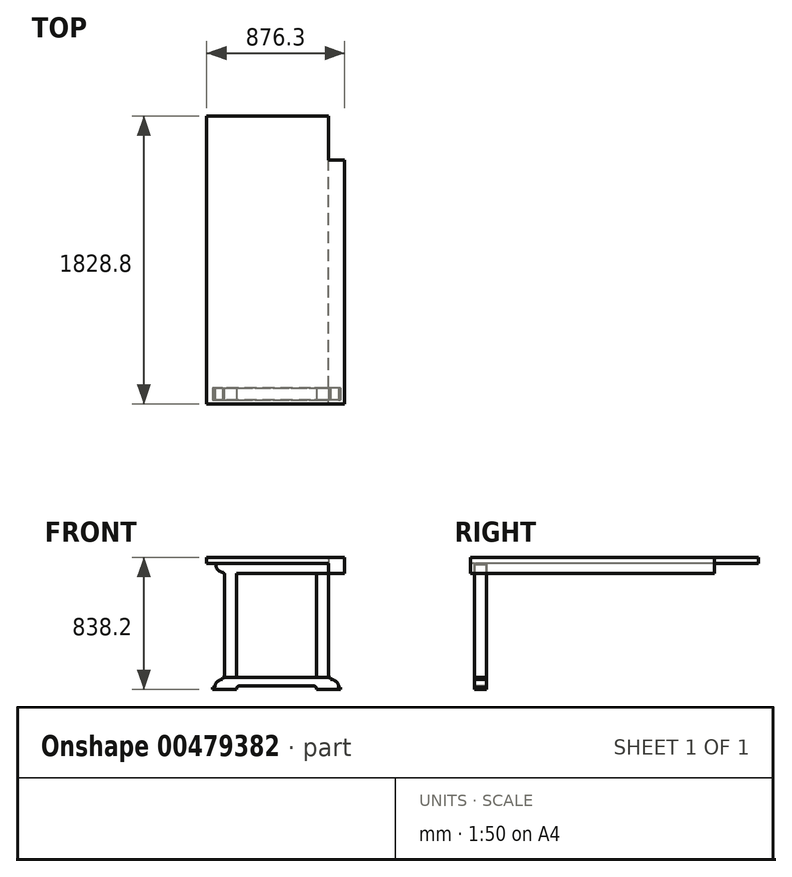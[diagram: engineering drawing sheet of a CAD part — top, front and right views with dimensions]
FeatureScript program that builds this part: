
annotation { "Feature Type Name" : "Feature", "Feature Type Description" : "" }
export const myFeature = defineFeature(function(context is Context, id is Id, definition is map)
    precondition{}
    {
        {
            var Q0;
            Q0=qCreatedBy(makeId("Front.planeOp"),FACE);
            var sketch = newSketch(context, id + "F0", { "sketchPlane" : qUnion([Q0])});
            skLineSegment(sketch, "E0.bottom", {"start": v(0, 0) * mm, "end": v(774.7, 0) * mm});
            skLineSegment(sketch, "E0.top", {"start": v(0, -38.1) * mm, "end": v(774.7, -38.1) * mm});
            skLineSegment(sketch, "E0.left", {"start": v(0, 0) * mm, "end": v(0, -38.1) * mm});
            skLineSegment(sketch, "E0.right", {"start": v(774.7, 0) * mm, "end": v(774.7, -38.1) * mm});
            skSolve(sketch);
        }
        {
            var Q0;
            Q0=qCreatedBy(makeId("Front.planeOp"),FACE);
            var sketch = newSketch(context, id + "F1", { "sketchPlane" : qUnion([Q0])});
            skLineSegment(sketch, "E1.bottom", {"start": v(774.7, 0) * mm, "end": v(876.3, 0) * mm});
            skLineSegment(sketch, "E1.top", {"start": v(774.7, -101.6) * mm, "end": v(876.3, -101.6) * mm});
            skLineSegment(sketch, "E1.left", {"start": v(774.7, 0) * mm, "end": v(774.7, -101.6) * mm});
            skLineSegment(sketch, "E1.right", {"start": v(876.3, 0) * mm, "end": v(876.3, -101.6) * mm});
            skSolve(sketch);
        }
        {
            var Q0;
            Q0=qCreatedBy(makeId("Front.planeOp"),FACE);
            var sketch = newSketch(context, id + "F2", { "sketchPlane" : qUnion([Q0])});
            skLineSegment(sketch, "E2.bottom", {"start": v(50.8, -38.1) * mm, "end": v(774.7, -38.1) * mm});
            skLineSegment(sketch, "E2.top", {"start": v(50.8, -101.6) * mm, "end": v(774.7, -101.6) * mm});
            skLineSegment(sketch, "E2.left", {"start": v(50.8, -38.1) * mm, "end": v(50.8, -101.6) * mm});
            skLineSegment(sketch, "E2.right", {"start": v(774.7, -38.1) * mm, "end": v(774.7, -101.6) * mm});
            skSolve(sketch);
        }
        {
            var Q0;
            Q0=qCreatedBy(makeId("Front.planeOp"),FACE);
            var sketch = newSketch(context, id + "F3", { "sketchPlane" : qUnion([Q0])});
            skCircle(sketch, "E3", {"center": v(107.95, -44.45) * mm, "radius": 50.8 * mm});
            skSolve(sketch);
        }
        {
            var Q0;
            Q0=qCreatedBy(makeId("Front.planeOp"),FACE);
            var sketch = newSketch(context, id + "F4", { "sketchPlane" : qUnion([Q0])});
            skLineSegment(sketch, "E4", {"start": v(107.47, -44.22) * mm, "end": v(48.14, -44.22) * mm});
            skLineSegment(sketch, "E5", {"start": v(107.47, -44.22) * mm, "end": v(107.47, -109.3) * mm});
            skSolve(sketch);
        }
        {
            var Q0;
            Q0=qCreatedBy(makeId("Front.planeOp"),FACE);
            var sketch = newSketch(context, id + "F5", { "sketchPlane" : qUnion([Q0])});
            skLineSegment(sketch, "E6.0", {"start": v(57.15, -44.22) * mm, "end": v(50.8, -44.22) * mm});
            skLineSegment(sketch, "E6.1", {"start": v(107.47, -95.25) * mm, "end": v(107.47, -101.6) * mm});
            skLineSegment(sketch, "E6.2", {"start": v(107.47, -101.6) * mm, "end": v(774.7, -101.6) * mm});
            skLineSegment(sketch, "E6.3", {"start": v(50.8, -38.1) * mm, "end": v(50.8, -44.22) * mm});
            skArc(sketch, "E6.4", {"start": v(57.15, -44.22) * mm, "mid": v(71.78, -80.12) * mm, "end": v(107.47, -95.25) * mm});
            skLineSegment(sketch, "E7.0.2", {"start": v(774.7, -101.6) * mm, "end": v(774.7, -38.1) * mm});
            skLineSegment(sketch, "E7.0.3", {"start": v(774.7, -38.1) * mm, "end": v(50.8, -38.1) * mm});
            skPoint(sketch, "E8.orphan", {"position": v(107.47, -109.3) * mm});
            skPoint(sketch, "E9.orphan", {"position": v(48.14, -44.22) * mm});
            skPoint(sketch, "E10.orphan", {"position": v(107.47, -44.22) * mm});
            skPoint(sketch, "E11.orphan", {"position": v(50.8, -101.6) * mm});
            skSolve(sketch);
        }
        {
            var Q0;
            Q0=qCreatedBy(makeId("Front.planeOp"),FACE);
            var sketch = newSketch(context, id + "F6", { "sketchPlane" : qUnion([Q0])});
            skPoint(sketch, "E12.0", {"position": v(50.8, -44.22) * mm});
            skLineSegment(sketch, "E12.1", {"start": v(107.47, -95.25) * mm, "end": v(107.47, -101.6) * mm});
            skLineSegment(sketch, "E12.2", {"start": v(107.47, -101.6) * mm, "end": v(774.7, -101.6) * mm});
            skPoint(sketch, "E13.orphan", {"position": v(107.47, -109.3) * mm});
            skSolve(sketch);
        }
        {
            var Q0;
            Q0=qSketchRegion(id+"F5",true);
            extrude(context, id + "F7", {"entities" : qUnion([Q0]), "depth" : 76.2 * mm});
        }
        {
            var Q0;
            Q0=makeQuery(id+"F0.imprint","IMPRINT",FACE,{"disambiguationData":[TD([[makeQuery(id+"F0.imprint","IMPRINT",EDGE,{"derivedFrom":sQuery(id+"F0.wireOp",EDGE,"E0.bottom")}),-1.0]])]});
            extrude(context, id + "F8", {"entities" : qUnion([Q0]), "operationType" : NewBodyOperationType.ADD, "oppositeDirection" : true, "depth" : 1727.2 * mm, "hasSecondDirection" : true, "secondDirectionOppositeDirection" : false, "secondDirectionDepth" : 101.6 * mm});
        }
        {
            var Q0;
            Q0=makeQuery(id+"F1.imprint","IMPRINT",FACE,{"disambiguationData":[TD([[makeQuery(id+"F1.imprint","IMPRINT",EDGE,{"derivedFrom":sQuery(id+"F1.wireOp",EDGE,"E1.bottom")}),-1.0]])]});
            extrude(context, id + "F9", {"entities" : qUnion([Q0]), "operationType" : NewBodyOperationType.ADD, "depth" : 101.6 * mm, "hasSecondDirection" : true, "secondDirectionOppositeDirection" : true, "secondDirectionDepth" : 1447.8 * mm});
        }
        {
            var Q0;
            Q0=qCreatedBy(makeId("Front.planeOp"),FACE);
            var sketch = newSketch(context, id + "F10", { "sketchPlane" : qUnion([Q0])});
            skLineSegment(sketch, "E14.bottom", {"start": v(114.3, -101.6) * mm, "end": v(190.5, -101.6) * mm});
            skLineSegment(sketch, "E14.top", {"start": v(114.3, -762) * mm, "end": v(190.5, -762) * mm});
            skLineSegment(sketch, "E14.left", {"start": v(114.3, -101.6) * mm, "end": v(114.3, -762) * mm});
            skLineSegment(sketch, "E14.right", {"start": v(190.5, -101.6) * mm, "end": v(190.5, -762) * mm});
            skSolve(sketch);
        }
        {
            var Q0;
            Q0=makeQuery(id+"F10.imprint","IMPRINT",FACE,{"disambiguationData":[TD([[makeQuery(id+"F10.imprint","IMPRINT",EDGE,{"derivedFrom":sQuery(id+"F10.wireOp",EDGE,"E14.bottom")}),-1.0]])]});
            extrude(context, id + "F11", {"entities" : qUnion([Q0]), "operationType" : NewBodyOperationType.ADD, "depth" : 76.2 * mm});
        }
        {
            var Q0;
            Q0=makeQuery(id+"F11.boolean.opBoolean","MERGE",FACE,{"derivedFrom":[makeQuery(id+"F7.opExtrude","CAP_FACE",FACE,{"disambiguationData":[OSD([sQuery(id+"F5.wireOp",EDGE,"E6.0"),sQuery(id+"F5.wireOp",EDGE,"E6.1"),sQuery(id+"F5.wireOp",EDGE,"E6.4"),sQuery(id+"F5.wireOp",EDGE,"E6.3"),sQuery(id+"F5.wireOp",EDGE,"E6.2"),sQuery(id+"F5.wireOp",EDGE,"E7.0.2"),sQuery(id+"F5.wireOp",EDGE,"E7.0.3")])],"isStart":false}),makeQuery(id+"F11.opExtrude","CAP_FACE",FACE,{"disambiguationData":[OSD([sQuery(id+"F10.wireOp",EDGE,"E14.bottom"),sQuery(id+"F10.wireOp",EDGE,"E14.top"),sQuery(id+"F10.wireOp",EDGE,"E14.left"),sQuery(id+"F10.wireOp",EDGE,"E14.right")])],"isStart":false})]});
            var sketch = newSketch(context, id + "F12", { "sketchPlane" : qUnion([Q0])});
            skLineSegment(sketch, "E15.bottom", {"start": v(698.5, -101.6) * mm, "end": v(774.7, -101.6) * mm});
            skLineSegment(sketch, "E15.top", {"start": v(698.5, -762) * mm, "end": v(774.7, -762) * mm});
            skLineSegment(sketch, "E15.left", {"start": v(698.5, -101.6) * mm, "end": v(698.5, -762) * mm});
            skLineSegment(sketch, "E15.right", {"start": v(774.7, -101.6) * mm, "end": v(774.7, -762) * mm});
            skSolve(sketch);
        }
        {
            var Q0;
            Q0=makeQuery(id+"F12.imprint","IMPRINT",FACE,{"disambiguationData":[TD([[makeQuery(id+"F12.imprint","IMPRINT",EDGE,{"derivedFrom":sQuery(id+"F12.wireOp",EDGE,"E15.bottom")}),-1.0]])]});
            extrude(context, id + "F13", {"entities" : qUnion([Q0]), "oppositeDirection" : true, "depth" : 76.2 * mm});
        }
        {
            var Q0;
            Q0=makeQuery(id+"F11.boolean.opBoolean","MERGE",FACE,{"derivedFrom":[makeQuery(id+"F7.opExtrude","CAP_FACE",FACE,{"disambiguationData":[OSD([sQuery(id+"F5.wireOp",EDGE,"E6.0"),sQuery(id+"F5.wireOp",EDGE,"E6.1"),sQuery(id+"F5.wireOp",EDGE,"E6.4"),sQuery(id+"F5.wireOp",EDGE,"E6.3"),sQuery(id+"F5.wireOp",EDGE,"E6.2"),sQuery(id+"F5.wireOp",EDGE,"E7.0.2"),sQuery(id+"F5.wireOp",EDGE,"E7.0.3")])],"isStart":false}),makeQuery(id+"F11.opExtrude","CAP_FACE",FACE,{"disambiguationData":[OSD([sQuery(id+"F10.wireOp",EDGE,"E14.bottom"),sQuery(id+"F10.wireOp",EDGE,"E14.top"),sQuery(id+"F10.wireOp",EDGE,"E14.left"),sQuery(id+"F10.wireOp",EDGE,"E14.right")])],"isStart":false})]});
            var sketch = newSketch(context, id + "F14", { "sketchPlane" : qUnion([Q0])});
            skLineSegment(sketch, "E16.bottom", {"start": v(101.6, -762) * mm, "end": v(444.5, -762) * mm});
            skLineSegment(sketch, "E16.top", {"start": v(38.1, -838.2) * mm, "end": v(190.5, -838.2) * mm});
            skLineSegment(sketch, "E16.left", {"start": v(38.1, -825.5) * mm, "end": v(38.1, -838.2) * mm});
            skArc(sketch, "E17", {"start": v(101.6, -774.7) * mm, "mid": v(65.68, -789.58) * mm, "end": v(50.8, -825.5) * mm});
            skLineSegment(sketch, "E18", {"start": v(50.8, -825.5) * mm, "end": v(38.1, -825.5) * mm});
            skLineSegment(sketch, "E19", {"start": v(101.6, -774.7) * mm, "end": v(101.6, -762) * mm});
            skPoint(sketch, "E20.orphan", {"position": v(38.1, -762) * mm});
            skLineSegment(sketch, "E21.MirrorCS", {"start": v(787.4, -762) * mm, "end": v(444.5, -762) * mm});
            skArc(sketch, "E22.MirrorCS", {"start": v(787.4, -774.7) * mm, "mid": v(823.32, -789.58) * mm, "end": v(838.2, -825.5) * mm});
            skLineSegment(sketch, "E23.MirrorCS", {"start": v(850.9, -838.2) * mm, "end": v(695.54, -838.2) * mm});
            skLineSegment(sketch, "E24.MirrorCS", {"start": v(787.4, -774.7) * mm, "end": v(787.4, -762) * mm});
            skLineSegment(sketch, "E25.MirrorCS", {"start": v(850.9, -825.5) * mm, "end": v(850.9, -838.2) * mm});
            skLineSegment(sketch, "E26.MirrorCS", {"start": v(838.2, -825.5) * mm, "end": v(850.9, -825.5) * mm});
            skLineSegment(sketch, "E27.bottom", {"start": v(203.2, -817.14) * mm, "end": v(682.84, -817.14) * mm});
            skLineSegment(sketch, "E27.left", {"start": v(190.5, -829.84) * mm, "end": v(190.5, -838.2) * mm});
            skLineSegment(sketch, "E27.right", {"start": v(695.54, -829.84) * mm, "end": v(695.54, -838.2) * mm});
            skPoint(sketch, "E28.visualSharp", {"position": v(190.5, -817.14) * mm});
            skArc(sketch, "E28.filletArc", {"start": v(203.2, -817.14) * mm, "mid": v(194.22, -820.86) * mm, "end": v(190.5, -829.84) * mm});
            skPoint(sketch, "E29.visualSharp", {"position": v(695.54, -817.14) * mm});
            skArc(sketch, "E29.filletArc", {"start": v(695.54, -829.84) * mm, "mid": v(691.82, -820.86) * mm, "end": v(682.84, -817.14) * mm});
            skSolve(sketch);
        }
        {
            var Q0;
            Q0=makeQuery(id+"F14.imprint","IMPRINT",FACE,{"disambiguationData":[TD([[makeQuery(id+"F14.imprint","IMPRINT",EDGE,{"derivedFrom":sQuery(id+"F14.wireOp",EDGE,"E16.top")}),1.0]])]});
            extrude(context, id + "F15", {"entities" : qUnion([Q0]), "oppositeDirection" : true, "depth" : 76.2 * mm});
        }
    });
